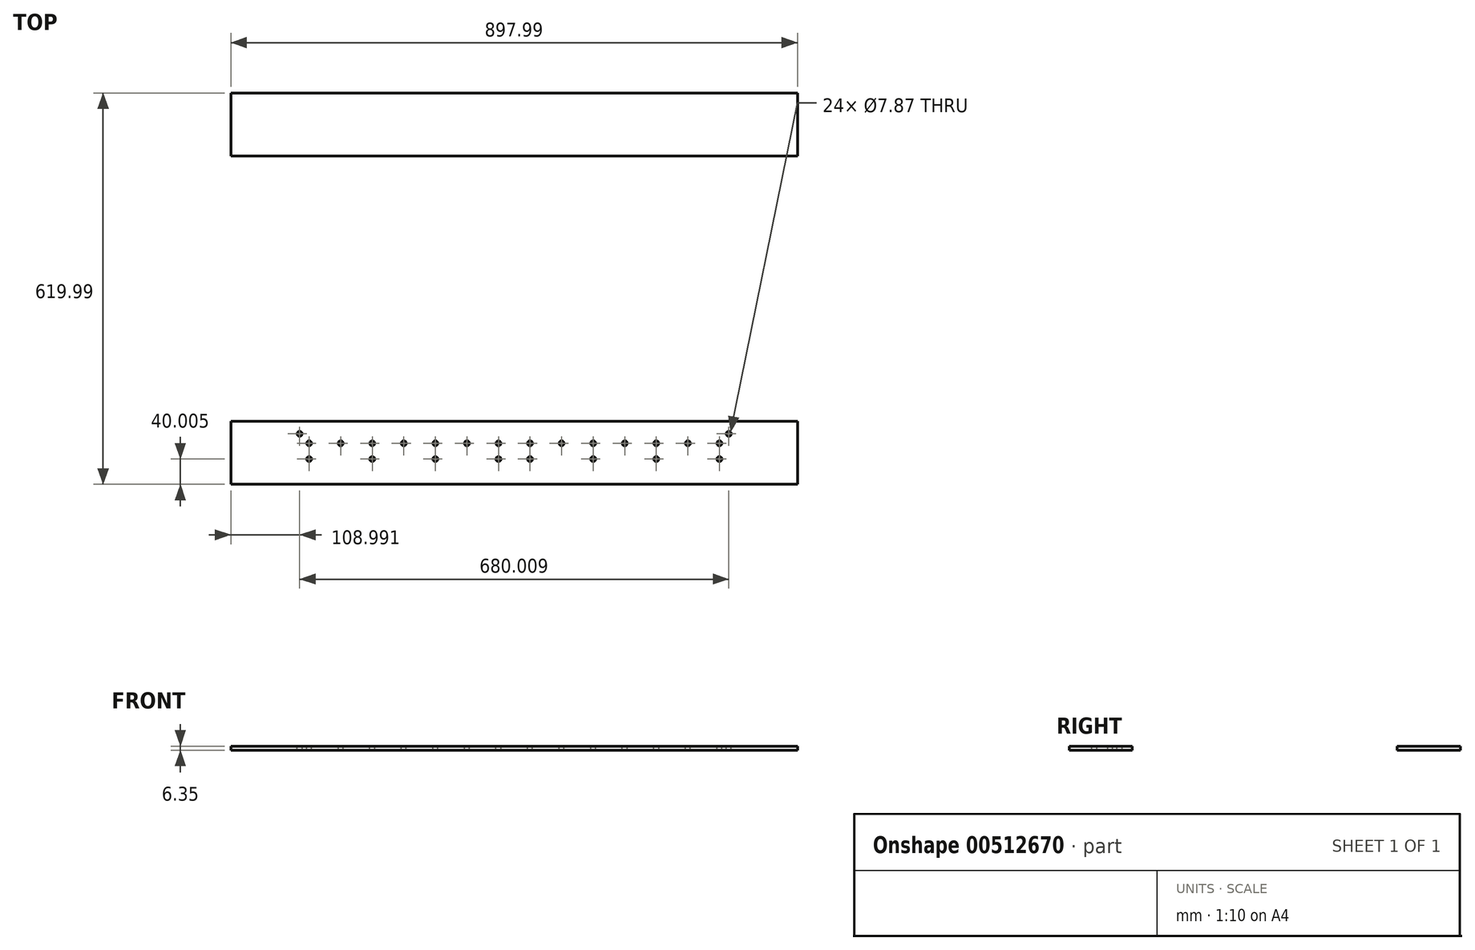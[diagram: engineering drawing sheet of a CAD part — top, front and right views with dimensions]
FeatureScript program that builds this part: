
annotation { "Feature Type Name" : "Feature", "Feature Type Description" : "" }
export const myFeature = defineFeature(function(context is Context, id is Id, definition is map)
    precondition{}
    {
        {
            var Q0;
            Q0=qCreatedBy(makeId("Top.planeOp"),FACE);
            var sketch = newSketch(context, id + "F0", { "sketchPlane" : qUnion([Q0])});
            skLineSegment(sketch, "E0.bottom", {"start": v(0, 0) * mm, "end": v(898, 0) * mm});
            skLineSegment(sketch, "E0.top", {"start": v(0, 100) * mm, "end": v(898, 100) * mm});
            skLineSegment(sketch, "E0.left", {"start": v(0, 0) * mm, "end": v(0, 100) * mm});
            skLineSegment(sketch, "E0.right", {"start": v(898, 0) * mm, "end": v(898, 100) * mm});
            skLineSegment(sketch, "E1.bottom", {"start": v(0, 100) * mm, "end": v(138.99, 100) * mm});
            skLineSegment(sketch, "E1.top", {"start": v(0, 519.99) * mm, "end": v(138.99, 519.99) * mm});
            skLineSegment(sketch, "E1.left", {"start": v(0, 100) * mm, "end": v(0, 519.99) * mm});
            skLineSegment(sketch, "E1.right", {"start": v(138.99, 100) * mm, "end": v(138.99, 519.99) * mm});
            skLineSegment(sketch, "E2.MirrorCS", {"start": v(898, 100) * mm, "end": v(759, 100) * mm});
            skLineSegment(sketch, "E3.MirrorCS", {"start": v(898, 100) * mm, "end": v(898, 519.99) * mm});
            skLineSegment(sketch, "E4.MirrorCS", {"start": v(898, 519.99) * mm, "end": v(759, 519.99) * mm});
            skLineSegment(sketch, "E5.MirrorCS", {"start": v(759, 100) * mm, "end": v(759, 519.99) * mm});
            skLineSegment(sketch, "E6.MirrorCS", {"start": v(0, 519.99) * mm, "end": v(898, 519.99) * mm});
            skLineSegment(sketch, "E7.MirrorCS", {"start": v(0, 619.99) * mm, "end": v(0, 519.99) * mm});
            skLineSegment(sketch, "E8.MirrorCS", {"start": v(0, 619.99) * mm, "end": v(898, 619.99) * mm});
            skLineSegment(sketch, "E9.MirrorCS", {"start": v(898, 619.99) * mm, "end": v(898, 519.99) * mm});
            skSolve(sketch);
        }
        {
            var Q0;
            Q0=makeQuery(id+"F0.imprint","IMPRINT",FACE,{"disambiguationData":[TD([[makeQuery(id+"F0.imprint","IMPRINT",EDGE,{"derivedFrom":sQuery(id+"F0.wireOp",EDGE,"E1.bottom")}),1.0]])]});
            var Q1;
            {var subQ0=sQuery(id+"F0.wireOp",EDGE,"E7.MirrorCS");Q1=makeQuery(id+"F0.imprint","IMPRINT",FACE,{"disambiguationData":[TD([[makeQuery(id+"F0.imprint","IMPRINT",EDGE,{"derivedFrom":subQ0}),1.0]])]});}
            var Q2;
            Q2=makeQuery(id+"F0.imprint","IMPRINT",FACE,{"disambiguationData":[TD([[makeQuery(id+"F0.imprint","IMPRINT",EDGE,{"derivedFrom":sQuery(id+"F0.wireOp",EDGE,"E2.MirrorCS")}),-1.0]])]});
            var Q3;
            Q3=makeQuery(id+"F0.imprint","IMPRINT",FACE,{"disambiguationData":[TD([[makeQuery(id+"F0.imprint","IMPRINT",EDGE,{"derivedFrom":sQuery(id+"F0.wireOp",EDGE,"E0.bottom")}),1.0]])]});
            extrude(context, id + "F1", {"entities" : qUnion([Q0, Q1, Q2, Q3]), "depth" : 6.35 * mm});
        }
        {
            var Q0;
            Q0=makeQuery(id+"F1.opExtrude","CAP_FACE",FACE,{"disambiguationData":[OSD([sQuery(id+"F0.wireOp",EDGE,"E0.bottom"),sQuery(id+"F0.wireOp",EDGE,"E0.top"),sQuery(id+"F0.wireOp",EDGE,"E0.left"),sQuery(id+"F0.wireOp",EDGE,"E0.right"),sQuery(id+"F0.wireOp",EDGE,"E1.left"),sQuery(id+"F0.wireOp",EDGE,"E1.right"),sQuery(id+"F0.wireOp",EDGE,"E3.MirrorCS"),sQuery(id+"F0.wireOp",EDGE,"E5.MirrorCS"),sQuery(id+"F0.wireOp",EDGE,"E6.MirrorCS"),sQuery(id+"F0.wireOp",EDGE,"E7.MirrorCS"),sQuery(id+"F0.wireOp",EDGE,"E8.MirrorCS"),sQuery(id+"F0.wireOp",EDGE,"E9.MirrorCS")])],"isStart":false});
            var sketch = newSketch(context, id + "F2", { "sketchPlane" : qUnion([Q0])});
            skLineSegment(sketch, "E10", {"start": v(0, 0) * mm, "end": v(124, 0) * mm});
            skLineSegment(sketch, "E11", {"start": v(124, 0) * mm, "end": v(124, 40) * mm});
            skLineSegment(sketch, "E12", {"start": v(124, 40) * mm, "end": v(124, 65) * mm});
            skCircle(sketch, "E13", {"center": v(124, 65) * mm, "radius": 3.94 * mm});
            skCircle(sketch, "E14.1.0.0", {"center": v(174.02, 65) * mm, "radius": 3.94 * mm});
            skCircle(sketch, "E14.2.0.0", {"center": v(224.03, 65) * mm, "radius": 3.94 * mm});
            skCircle(sketch, "E14.3.0.0", {"center": v(274.04, 65) * mm, "radius": 3.94 * mm});
            skCircle(sketch, "E14.4.0.0", {"center": v(324.05, 65) * mm, "radius": 3.94 * mm});
            skCircle(sketch, "E14.5.0.0", {"center": v(374.07, 65) * mm, "radius": 3.94 * mm});
            skCircle(sketch, "E14.6.0.0", {"center": v(424.08, 65) * mm, "radius": 3.94 * mm});
            skCircle(sketch, "E14.7.0.0", {"center": v(474.1, 65) * mm, "radius": 3.94 * mm});
            skCircle(sketch, "E14.8.0.0", {"center": v(524.1, 65) * mm, "radius": 3.94 * mm});
            skCircle(sketch, "E14.9.0.0", {"center": v(574.12, 65) * mm, "radius": 3.94 * mm});
            skCircle(sketch, "E14.10.0.0", {"center": v(624.13, 65) * mm, "radius": 3.94 * mm});
            skCircle(sketch, "E14.11.0.0", {"center": v(674.14, 65) * mm, "radius": 3.94 * mm});
            skCircle(sketch, "E14.12.0.0", {"center": v(724.15, 65) * mm, "radius": 3.94 * mm});
            skCircle(sketch, "E14.13.0.0", {"center": v(774.17, 65) * mm, "radius": 3.94 * mm});
            skLineSegment(sketch, "E14.direction1", {"start": v(124, 65) * mm, "end": v(174.02, 65) * mm, "construction": true});
            skLineSegment(sketch, "E15", {"start": v(138.99, 310) * mm, "end": v(268.02, 310) * mm});
            skPoint(sketch, "E15.endSnap0", {"position": v(138.99, 310) * mm});
            skCircle(sketch, "E16", {"center": v(124, 40) * mm, "radius": 3.94 * mm});
            skCircle(sketch, "E17.1.0.0", {"center": v(224.03, 40) * mm, "radius": 3.94 * mm});
            skCircle(sketch, "E17.2.0.0", {"center": v(324.05, 40) * mm, "radius": 3.94 * mm});
            skCircle(sketch, "E17.3.0.0", {"center": v(424.08, 40) * mm, "radius": 3.94 * mm});
            skLineSegment(sketch, "E17.direction1", {"start": v(124, 40) * mm, "end": v(224.03, 40) * mm, "construction": true});
            skLineSegment(sketch, "E18", {"start": v(424.08, 40) * mm, "end": v(474.1, 40) * mm});
            skCircle(sketch, "E19", {"center": v(474.1, 40) * mm, "radius": 3.94 * mm});
            skCircle(sketch, "E20.1.0.0", {"center": v(574.12, 40) * mm, "radius": 3.94 * mm});
            skCircle(sketch, "E20.2.0.0", {"center": v(674.14, 40) * mm, "radius": 3.94 * mm});
            skCircle(sketch, "E20.3.0.0", {"center": v(774.17, 40) * mm, "radius": 3.94 * mm});
            skLineSegment(sketch, "E20.direction1", {"start": v(474.1, 40) * mm, "end": v(574.12, 40) * mm, "construction": true});
            skCircle(sketch, "E21.MirrorC", {"center": v(124, 579.98) * mm, "radius": 3.94 * mm});
            skCircle(sketch, "E22.MirrorC", {"center": v(124, 555) * mm, "radius": 3.94 * mm});
            skCircle(sketch, "E23.MirrorC", {"center": v(174.02, 555) * mm, "radius": 3.94 * mm});
            skCircle(sketch, "E24.MirrorC", {"center": v(224.03, 555) * mm, "radius": 3.94 * mm});
            skCircle(sketch, "E25.MirrorC", {"center": v(224.03, 579.98) * mm, "radius": 3.94 * mm});
            skCircle(sketch, "E26.MirrorC", {"center": v(274.04, 555) * mm, "radius": 3.94 * mm});
            skCircle(sketch, "E27.MirrorC", {"center": v(324.05, 555) * mm, "radius": 3.94 * mm});
            skCircle(sketch, "E28.MirrorC", {"center": v(324.05, 579.98) * mm, "radius": 3.94 * mm});
            skCircle(sketch, "E29.MirrorC", {"center": v(374.07, 555) * mm, "radius": 3.94 * mm});
            skCircle(sketch, "E30.MirrorC", {"center": v(424.08, 555) * mm, "radius": 3.94 * mm});
            skCircle(sketch, "E31.MirrorC", {"center": v(424.08, 579.98) * mm, "radius": 3.94 * mm});
            skCircle(sketch, "E32.MirrorC", {"center": v(474.1, 555) * mm, "radius": 3.94 * mm});
            skCircle(sketch, "E33.MirrorC", {"center": v(474.1, 579.98) * mm, "radius": 3.94 * mm});
            skCircle(sketch, "E34.MirrorC", {"center": v(524.1, 555) * mm, "radius": 3.94 * mm});
            skCircle(sketch, "E35.MirrorC", {"center": v(624.13, 555) * mm, "radius": 3.94 * mm});
            skCircle(sketch, "E36.MirrorC", {"center": v(674.14, 555) * mm, "radius": 3.94 * mm});
            skCircle(sketch, "E37.MirrorC", {"center": v(674.14, 579.98) * mm, "radius": 3.94 * mm});
            skCircle(sketch, "E38.MirrorC", {"center": v(724.15, 555) * mm, "radius": 3.94 * mm});
            skCircle(sketch, "E39.MirrorC", {"center": v(774.17, 555) * mm, "radius": 3.94 * mm});
            skCircle(sketch, "E40.MirrorC", {"center": v(774.17, 579.98) * mm, "radius": 3.94 * mm});
            skCircle(sketch, "E41.MirrorC", {"center": v(574.12, 555) * mm, "radius": 3.94 * mm});
            skCircle(sketch, "E42.MirrorC", {"center": v(574.12, 579.98) * mm, "radius": 3.94 * mm});
            skLineSegment(sketch, "E43", {"start": v(124, 65) * mm, "end": v(109, 65) * mm});
            skLineSegment(sketch, "E44", {"start": v(109, 65) * mm, "end": v(109, 80) * mm});
            skCircle(sketch, "E45", {"center": v(109, 80) * mm, "radius": 3.94 * mm});
            skLineSegment(sketch, "E46", {"start": v(449, 100) * mm, "end": v(449, 150.02) * mm});
            skCircle(sketch, "E47.MirrorC", {"center": v(789, 80) * mm, "radius": 3.94 * mm});
            skCircle(sketch, "E48.MirrorC", {"center": v(109, 539.98) * mm, "radius": 3.94 * mm});
            skCircle(sketch, "E49.MirrorC", {"center": v(789, 539.98) * mm, "radius": 3.94 * mm});
            skCircle(sketch, "E50.0.1.0", {"center": v(109, 130.02) * mm, "radius": 3.94 * mm});
            skCircle(sketch, "E50.0.2.0", {"center": v(109, 180.04) * mm, "radius": 3.94 * mm});
            skCircle(sketch, "E50.0.3.0", {"center": v(109, 230.05) * mm, "radius": 3.94 * mm});
            skCircle(sketch, "E50.0.4.0", {"center": v(109, 280.06) * mm, "radius": 3.94 * mm});
            skCircle(sketch, "E50.0.5.0", {"center": v(109, 330.07) * mm, "radius": 3.94 * mm});
            skCircle(sketch, "E50.0.6.0", {"center": v(109, 380.09) * mm, "radius": 3.94 * mm});
            skCircle(sketch, "E50.0.7.0", {"center": v(109, 430.1) * mm, "radius": 3.94 * mm});
            skCircle(sketch, "E50.0.8.0", {"center": v(109, 480.11) * mm, "radius": 3.94 * mm});
            skLineSegment(sketch, "E50.direction1", {"start": v(109, 80) * mm, "end": v(134.4, 80) * mm, "construction": true});
            skLineSegment(sketch, "E50.direction2", {"start": v(109, 80) * mm, "end": v(109, 130.02) * mm, "construction": true});
            skLineSegment(sketch, "E51", {"start": v(109, 130.02) * mm, "end": v(84, 130.02) * mm});
            skLineSegment(sketch, "E52", {"start": v(84, 130.02) * mm, "end": v(84, 145.03) * mm});
            skCircle(sketch, "E53", {"center": v(84, 145.03) * mm, "radius": 3.94 * mm});
            skCircle(sketch, "E54.0.1.0", {"center": v(84, 225.04) * mm, "radius": 3.94 * mm});
            skCircle(sketch, "E54.0.2.0", {"center": v(84, 305.05) * mm, "radius": 3.94 * mm});
            skCircle(sketch, "E54.0.3.0", {"center": v(84, 385.06) * mm, "radius": 3.94 * mm});
            skCircle(sketch, "E54.0.4.0", {"center": v(84, 465.07) * mm, "radius": 3.94 * mm});
            skLineSegment(sketch, "E54.direction1", {"start": v(84, 145.03) * mm, "end": v(109.4, 145.03) * mm, "construction": true});
            skLineSegment(sketch, "E54.direction2", {"start": v(84, 145.03) * mm, "end": v(84, 225.04) * mm, "construction": true});
            skCircle(sketch, "E55.MirrorC", {"center": v(789, 480.11) * mm, "radius": 3.94 * mm});
            skCircle(sketch, "E56.MirrorC", {"center": v(814, 465.07) * mm, "radius": 3.94 * mm});
            skCircle(sketch, "E57.MirrorC", {"center": v(789, 430.1) * mm, "radius": 3.94 * mm});
            skCircle(sketch, "E58.MirrorC", {"center": v(814, 385.06) * mm, "radius": 3.94 * mm});
            skCircle(sketch, "E59.MirrorC", {"center": v(789, 380.09) * mm, "radius": 3.94 * mm});
            skCircle(sketch, "E60.MirrorC", {"center": v(789, 330.07) * mm, "radius": 3.94 * mm});
            skCircle(sketch, "E61.MirrorC", {"center": v(814, 305.05) * mm, "radius": 3.94 * mm});
            skCircle(sketch, "E62.MirrorC", {"center": v(789, 280.06) * mm, "radius": 3.94 * mm});
            skCircle(sketch, "E63.MirrorC", {"center": v(789, 130.02) * mm, "radius": 3.94 * mm});
            skCircle(sketch, "E64.MirrorC", {"center": v(814, 145.03) * mm, "radius": 3.94 * mm});
            skCircle(sketch, "E65.MirrorC", {"center": v(789, 180.04) * mm, "radius": 3.94 * mm});
            skCircle(sketch, "E66.MirrorC", {"center": v(814, 225.04) * mm, "radius": 3.94 * mm});
            skCircle(sketch, "E67.MirrorC", {"center": v(789, 230.05) * mm, "radius": 3.94 * mm});
            skSolve(sketch);
        }
        {
            var Q0;
            Q0=sQuery(id+"F2.wireOp",VERTEX,"E48.MirrorC.center");
            var Q1;
            Q1=sQuery(id+"F2.wireOp",VERTEX,"E22.MirrorC.center");
            var Q2;
            Q2=sQuery(id+"F2.wireOp",VERTEX,"E23.MirrorC.center");
            var Q3;
            Q3=sQuery(id+"F2.wireOp",VERTEX,"E21.MirrorC.center");
            var Q4;
            Q4=sQuery(id+"F2.wireOp",VERTEX,"E25.MirrorC.center");
            var Q5;
            Q5=sQuery(id+"F2.wireOp",VERTEX,"E24.MirrorC.center");
            var Q6;
            Q6=sQuery(id+"F2.wireOp",VERTEX,"E26.MirrorC.center");
            var Q7;
            Q7=sQuery(id+"F2.wireOp",VERTEX,"E28.MirrorC.center");
            var Q8;
            Q8=sQuery(id+"F2.wireOp",VERTEX,"E27.MirrorC.center");
            var Q9;
            Q9=sQuery(id+"F2.wireOp",VERTEX,"E29.MirrorC.center");
            var Q10;
            Q10=sQuery(id+"F2.wireOp",VERTEX,"E31.MirrorC.center");
            var Q11;
            Q11=sQuery(id+"F2.wireOp",VERTEX,"E30.MirrorC.center");
            var Q12;
            Q12=sQuery(id+"F2.wireOp",VERTEX,"E33.MirrorC.center");
            var Q13;
            Q13=sQuery(id+"F2.wireOp",VERTEX,"E32.MirrorC.center");
            var Q14;
            Q14=sQuery(id+"F2.wireOp",VERTEX,"E34.MirrorC.center");
            var Q15;
            Q15=sQuery(id+"F2.wireOp",VERTEX,"E42.MirrorC.center");
            var Q16;
            Q16=sQuery(id+"F2.wireOp",VERTEX,"E41.MirrorC.center");
            var Q17;
            Q17=sQuery(id+"F2.wireOp",VERTEX,"E35.MirrorC.center");
            var Q18;
            Q18=sQuery(id+"F2.wireOp",VERTEX,"E37.MirrorC.center");
            var Q19;
            Q19=sQuery(id+"F2.wireOp",VERTEX,"E36.MirrorC.center");
            var Q20;
            Q20=sQuery(id+"F2.wireOp",VERTEX,"E49.MirrorC.center");
            var Q21;
            Q21=sQuery(id+"F2.wireOp",VERTEX,"E40.MirrorC.center");
            var Q22;
            Q22=sQuery(id+"F2.wireOp",VERTEX,"E39.MirrorC.center");
            var Q23;
            Q23=sQuery(id+"F2.wireOp",VERTEX,"E38.MirrorC.center");
            var Q24;
            Q24=sQuery(id+"F2.wireOp",VERTEX,"E55.MirrorC.center");
            var Q25;
            Q25=sQuery(id+"F2.wireOp",VERTEX,"E56.MirrorC.center");
            var Q26;
            Q26=sQuery(id+"F2.wireOp",VERTEX,"E63.MirrorC.center");
            var Q27;
            Q27=sQuery(id+"F2.wireOp",VERTEX,"E64.MirrorC.center");
            var Q28;
            Q28=sQuery(id+"F2.wireOp",VERTEX,"E65.MirrorC.center");
            var Q29;
            Q29=sQuery(id+"F2.wireOp",VERTEX,"E67.MirrorC.center");
            var Q30;
            Q30=sQuery(id+"F2.wireOp",VERTEX,"E66.MirrorC.center");
            var Q31;
            Q31=sQuery(id+"F2.wireOp",VERTEX,"E62.MirrorC.center");
            var Q32;
            Q32=sQuery(id+"F2.wireOp",VERTEX,"E61.MirrorC.center");
            var Q33;
            Q33=sQuery(id+"F2.wireOp",VERTEX,"E60.MirrorC.center");
            var Q34;
            Q34=sQuery(id+"F2.wireOp",VERTEX,"E59.MirrorC.center");
            var Q35;
            Q35=sQuery(id+"F2.wireOp",VERTEX,"E58.MirrorC.center");
            var Q36;
            Q36=sQuery(id+"F2.wireOp",VERTEX,"E57.MirrorC.center");
            var Q37;
            Q37=sQuery(id+"F2.wireOp",VERTEX,"E47.MirrorC.center");
            var Q38;
            Q38=sQuery(id+"F2.wireOp",VERTEX,"E14.13.0.0.center");
            var Q39;
            Q39=sQuery(id+"F2.wireOp",VERTEX,"E20.3.0.0.center");
            var Q40;
            Q40=sQuery(id+"F2.wireOp",VERTEX,"E14.12.0.0.center");
            var Q41;
            Q41=sQuery(id+"F2.wireOp",VERTEX,"E14.11.0.0.center");
            var Q42;
            Q42=sQuery(id+"F2.wireOp",VERTEX,"E20.2.0.0.center");
            var Q43;
            Q43=sQuery(id+"F2.wireOp",VERTEX,"E54.0.4.0.center");
            var Q44;
            Q44=sQuery(id+"F2.wireOp",VERTEX,"E50.0.8.0.center");
            var Q45;
            Q45=sQuery(id+"F2.wireOp",VERTEX,"E50.0.7.0.center");
            var Q46;
            Q46=sQuery(id+"F2.wireOp",VERTEX,"E54.0.3.0.center");
            var Q47;
            Q47=sQuery(id+"F2.wireOp",VERTEX,"E50.0.6.0.center");
            var Q48;
            Q48=sQuery(id+"F2.wireOp",VERTEX,"E50.0.5.0.center");
            var Q49;
            Q49=sQuery(id+"F2.wireOp",VERTEX,"E54.0.2.0.center");
            var Q50;
            Q50=sQuery(id+"F2.wireOp",VERTEX,"E50.0.4.0.center");
            var Q51;
            Q51=sQuery(id+"F2.wireOp",VERTEX,"E54.direction2.end");
            var Q52;
            Q52=sQuery(id+"F2.wireOp",VERTEX,"E50.0.3.0.center");
            var Q53;
            Q53=sQuery(id+"F2.wireOp",VERTEX,"E50.0.2.0.center");
            var Q54;
            Q54=sQuery(id+"F2.wireOp",VERTEX,"E53.center");
            var Q55;
            Q55=sQuery(id+"F2.wireOp",VERTEX,"E51.start");
            var Q56;
            Q56=sQuery(id+"F2.wireOp",VERTEX,"E50.direction2.start");
            var Q57;
            Q57=sQuery(id+"F2.wireOp",VERTEX,"E14.direction1.start");
            var Q58;
            Q58=sQuery(id+"F2.wireOp",VERTEX,"E17.direction1.start");
            var Q59;
            Q59=sQuery(id+"F2.wireOp",VERTEX,"E14.direction1.end");
            var Q60;
            Q60=sQuery(id+"F2.wireOp",VERTEX,"E17.direction1.end");
            var Q61;
            Q61=sQuery(id+"F2.wireOp",VERTEX,"E14.2.0.0.center");
            var Q62;
            Q62=sQuery(id+"F2.wireOp",VERTEX,"E14.3.0.0.center");
            var Q63;
            Q63=sQuery(id+"F2.wireOp",VERTEX,"E17.2.0.0.center");
            var Q64;
            Q64=sQuery(id+"F2.wireOp",VERTEX,"E14.4.0.0.center");
            var Q65;
            Q65=sQuery(id+"F2.wireOp",VERTEX,"E14.5.0.0.center");
            var Q66;
            Q66=sQuery(id+"F2.wireOp",VERTEX,"E14.6.0.0.center");
            var Q67;
            Q67=sQuery(id+"F2.wireOp",VERTEX,"E18.start");
            var Q68;
            Q68=sQuery(id+"F2.wireOp",VERTEX,"E14.7.0.0.center");
            var Q69;
            Q69=sQuery(id+"F2.wireOp",VERTEX,"E20.direction1.start");
            var Q70;
            Q70=sQuery(id+"F2.wireOp",VERTEX,"E14.8.0.0.center");
            var Q71;
            Q71=sQuery(id+"F2.wireOp",VERTEX,"E14.9.0.0.center");
            var Q72;
            Q72=sQuery(id+"F2.wireOp",VERTEX,"E14.10.0.0.center");
            var Q73;
            Q73=sQuery(id+"F2.wireOp",VERTEX,"E20.direction1.end");
            var Q74;
            Q74=makeQuery(id+"F1.opExtrude","SWEPT_BODY",BODY,{"disambiguationData":[OSD([sQuery(id+"F0.wireOp",EDGE,"E0.bottom"),sQuery(id+"F0.wireOp",EDGE,"E0.top"),sQuery(id+"F0.wireOp",EDGE,"E0.left"),sQuery(id+"F0.wireOp",EDGE,"E0.right"),sQuery(id+"F0.wireOp",EDGE,"E1.left"),sQuery(id+"F0.wireOp",EDGE,"E1.right"),sQuery(id+"F0.wireOp",EDGE,"E3.MirrorCS"),sQuery(id+"F0.wireOp",EDGE,"E5.MirrorCS"),sQuery(id+"F0.wireOp",EDGE,"E6.MirrorCS"),sQuery(id+"F0.wireOp",EDGE,"E7.MirrorCS"),sQuery(id+"F0.wireOp",EDGE,"E8.MirrorCS"),sQuery(id+"F0.wireOp",EDGE,"E9.MirrorCS")])]});
            hole(context, id + "F3", {"style" : HoleStyle.SIMPLE, "endStyle" : HoleEndStyle.THROUGH, "holeDiameter" : 7.87 * mm, "isTappedThrough" : true, "tappedDepth" : 12.7 * mm, "tapClearance" : 3, "locations" : qUnion([Q0, Q1, Q2, Q3, Q4, Q5, Q6, Q7, Q8, Q9, Q10, Q11, Q12, Q13, Q14, Q15, Q16, Q17, Q18, Q19, Q20, Q21, Q22, Q23, Q24, Q25, Q26, Q27, Q28, Q29, Q30, Q31, Q32, Q33, Q34, Q35, Q36, Q37, Q38, Q39, Q40, Q41, Q42, Q43, Q44, Q45, Q46, Q47, Q48, Q49, Q50, Q51, Q52, Q53, Q54, Q55, Q56, Q57, Q58, Q59, Q60, Q61, Q62, Q63, Q64, Q65, Q66, Q67, Q68, Q69, Q70, Q71, Q72, Q73]), "scope" : qUnion([Q74])});
        }
    });
